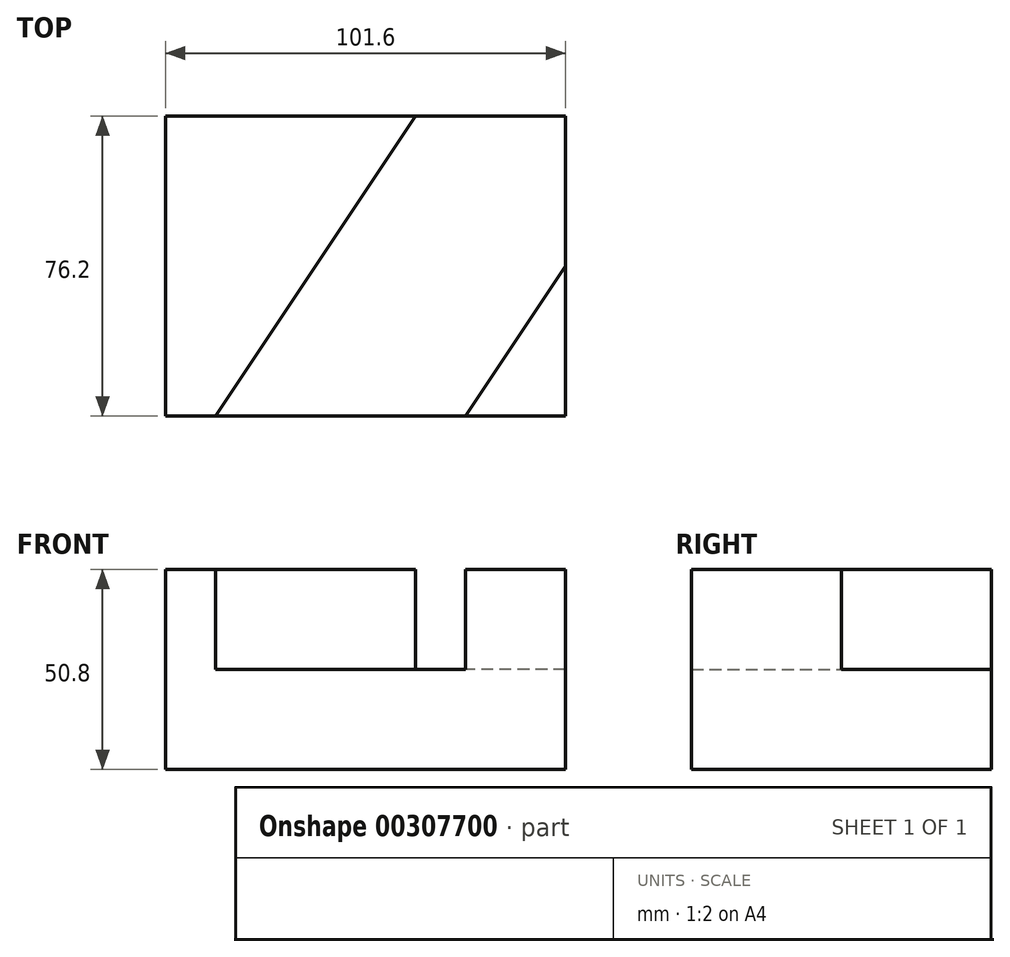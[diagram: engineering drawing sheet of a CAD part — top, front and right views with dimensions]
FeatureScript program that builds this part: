
annotation { "Feature Type Name" : "Feature", "Feature Type Description" : "" }
export const myFeature = defineFeature(function(context is Context, id is Id, definition is map)
    precondition{}
    {
        {
            var Q0;
            Q0=qCreatedBy(makeId("Top.planeOp"),FACE);
            var sketch = newSketch(context, id + "F0", { "sketchPlane" : qUnion([Q0])});
            skLineSegment(sketch, "E0", {"start": v(-43.08, 52.42) * mm, "end": v(-43.08, -23.78) * mm});
            skLineSegment(sketch, "E1", {"start": v(-43.08, -23.78) * mm, "end": v(58.52, -23.78) * mm});
            skLineSegment(sketch, "E2", {"start": v(58.52, -23.78) * mm, "end": v(58.52, 52.42) * mm});
            skLineSegment(sketch, "E3", {"start": v(58.52, 52.42) * mm, "end": v(-43.08, 52.42) * mm});
            skSolve(sketch);
        }
        {
            var Q0;
            Q0=makeQuery(id+"F0.imprint","IMPRINT",FACE,{"disambiguationData":[TD([[makeQuery(id+"F0.imprint","IMPRINT",EDGE,{"derivedFrom":sQuery(id+"F0.wireOp",EDGE,"E0")}),1.0]])]});
            extrude(context, id + "F1", {"entities" : qUnion([Q0]), "depth" : 25.4 * mm});
        }
        {
            var Q0;
            Q0=makeQuery(id+"F1.opExtrude","CAP_FACE",FACE,{"disambiguationData":[OSD([sQuery(id+"F0.wireOp",EDGE,"E0"),sQuery(id+"F0.wireOp",EDGE,"E1"),sQuery(id+"F0.wireOp",EDGE,"E2"),sQuery(id+"F0.wireOp",EDGE,"E3")])],"isStart":false});
            var sketch = newSketch(context, id + "F2", { "sketchPlane" : qUnion([Q0])});
            skLineSegment(sketch, "E4", {"start": v(58.52, 14.32) * mm, "end": v(33.12, -23.78) * mm});
            skLineSegment(sketch, "E5", {"start": v(33.12, -23.78) * mm, "end": v(58.52, -23.78) * mm});
            skLineSegment(sketch, "E6", {"start": v(58.52, -23.78) * mm, "end": v(58.52, 14.32) * mm});
            skSolve(sketch);
        }
        {
            var Q0;
            Q0 = qSketchRegion(id + "F2", true);
            extrude(context, id + "F3", {"entities" : qUnion([Q0]), "operationType" : NewBodyOperationType.ADD, "depth" : 25.4 * mm});
        }
        {
            var Q0;
            Q0=makeQuery(id+"F1.opExtrude","CAP_FACE",FACE,{"disambiguationData":[OSD([sQuery(id+"F0.wireOp",EDGE,"E0"),sQuery(id+"F0.wireOp",EDGE,"E1"),sQuery(id+"F0.wireOp",EDGE,"E2"),sQuery(id+"F0.wireOp",EDGE,"E3")])],"isStart":false});
            var sketch = newSketch(context, id + "F4", { "sketchPlane" : qUnion([Q0])});
            skLineSegment(sketch, "E7", {"start": v(-30.38, -23.78) * mm, "end": v(20.42, 52.42) * mm});
            skLineSegment(sketch, "E8", {"start": v(20.42, 52.42) * mm, "end": v(-43.08, 52.42) * mm});
            skLineSegment(sketch, "E9", {"start": v(-43.08, 52.42) * mm, "end": v(-43.08, -23.78) * mm});
            skLineSegment(sketch, "E10", {"start": v(-43.08, -23.78) * mm, "end": v(-30.38, -23.78) * mm});
            skSolve(sketch);
        }
        {
            var Q0;
            Q0=makeQuery(id+"F4.imprint","IMPRINT",FACE,{"disambiguationData":[TD([[makeQuery(id+"F4.imprint","IMPRINT",EDGE,{"derivedFrom":sQuery(id+"F4.wireOp",EDGE,"E7")}),1.0]])]});
            extrude(context, id + "F5", {"entities" : qUnion([Q0]), "operationType" : NewBodyOperationType.ADD, "depth" : 25.4 * mm});
        }
    });
